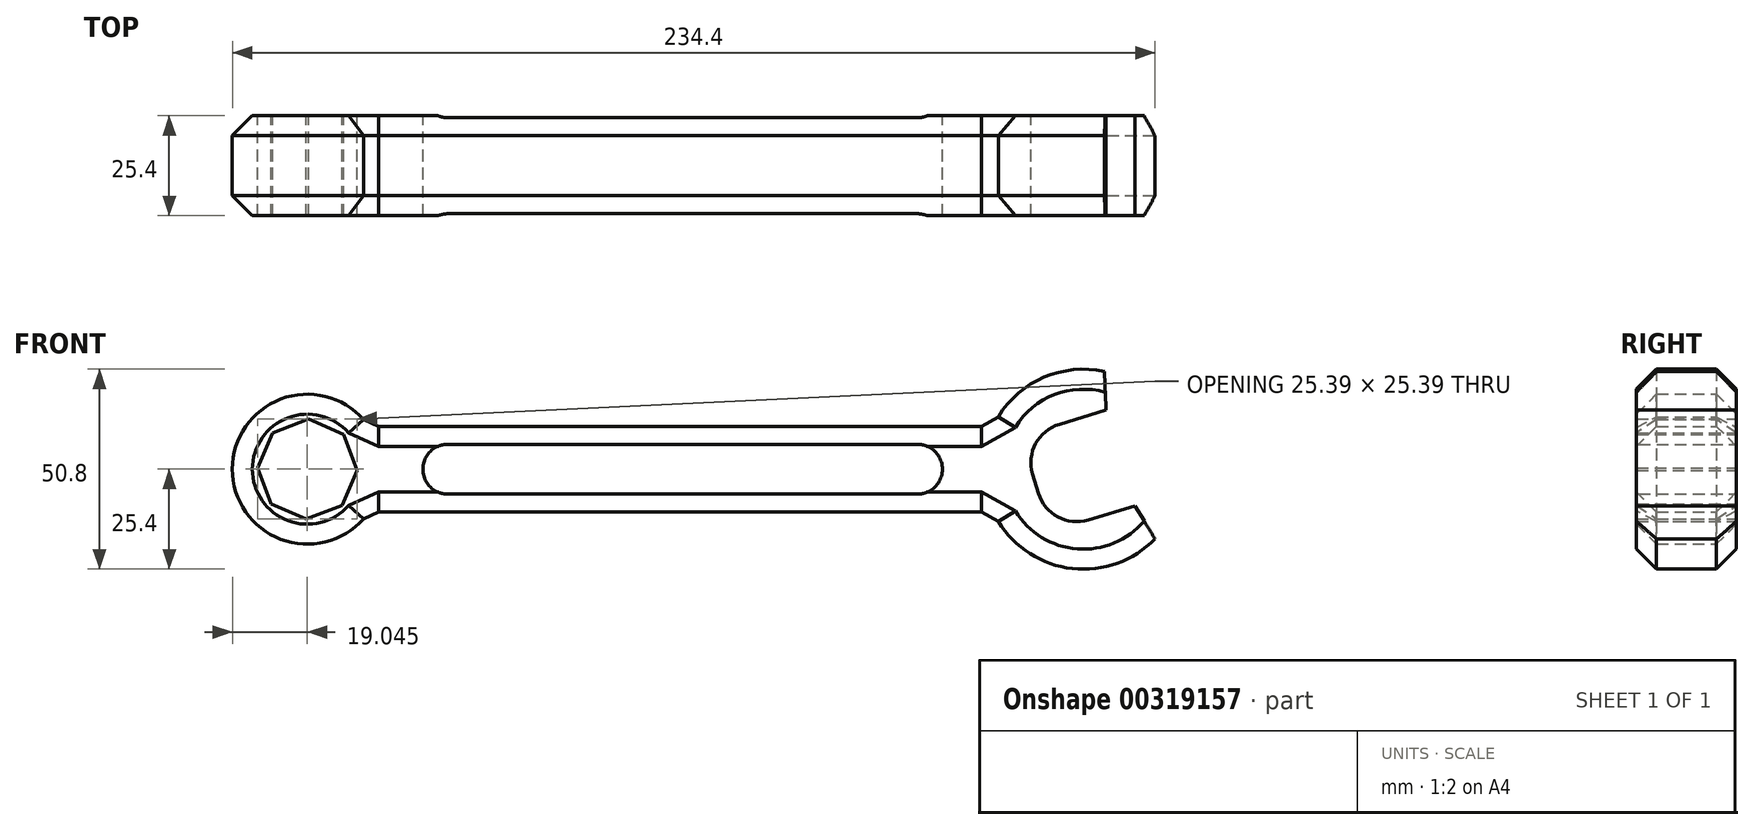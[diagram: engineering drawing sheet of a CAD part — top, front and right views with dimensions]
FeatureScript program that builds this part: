
annotation { "Feature Type Name" : "Feature", "Feature Type Description" : "" }
export const myFeature = defineFeature(function(context is Context, id is Id, definition is map)
    precondition{}
    {
        {
            var Q0;
            Q0=qCreatedBy(makeId("Front.planeOp"),FACE);
            var sketch = newSketch(context, id + "F0", { "sketchPlane" : qUnion([Q0])});
            skCircle(sketch, "E0", {"center": v(-95.33, 0) * mm, "radius": 19.05 * mm});
            skArc(sketch, "E1", {"start": v(119.2, 18.52) * mm, "mid": v(77.5, -7.35) * mm, "end": v(126.55, -5.8) * mm});
            skLineSegment(sketch, "E2", {"start": v(-79.71, 10.9) * mm, "end": v(78.88, 10.9) * mm});
            skLineSegment(sketch, "E3.MirrorCS", {"start": v(-79.71, -10.9) * mm, "end": v(78.88, -10.9) * mm});
            skCircle(sketch, "E4.cCircle", {"center": v(-95.33, 0) * mm, "radius": 12.7 * mm, "construction": true});
            skLineSegment(sketch, "E4.0", {"start": v(-86.54, -9.16) * mm, "end": v(-95.6, -12.7) * mm});
            skLineSegment(sketch, "E4.1", {"start": v(-95.6, -12.7) * mm, "end": v(-104.5, -8.8) * mm});
            skLineSegment(sketch, "E4.2", {"start": v(-104.5, -8.8) * mm, "end": v(-108.03, 0.26) * mm});
            skLineSegment(sketch, "E4.3", {"start": v(-108.03, 0.26) * mm, "end": v(-104.13, 9.16) * mm});
            skLineSegment(sketch, "E4.4", {"start": v(-104.13, 9.16) * mm, "end": v(-95.08, 12.7) * mm});
            skLineSegment(sketch, "E4.5", {"start": v(-95.08, 12.7) * mm, "end": v(-86.17, 8.8) * mm});
            skLineSegment(sketch, "E4.6", {"start": v(-86.17, 8.8) * mm, "end": v(-82.64, -0.26) * mm});
            skLineSegment(sketch, "E4.7", {"start": v(-82.64, -0.26) * mm, "end": v(-86.54, -9.16) * mm});
            skArc(sketch, "E5.cCircle", {"start": v(98.14, 12.16) * mm, "mid": v(89.66, -3.68) * mm, "end": v(105.5, -12.16) * mm, "construction": true});
            skLineSegment(sketch, "E5.1", {"start": v(117.65, -8.48) * mm, "end": v(103.06, -12.9) * mm});
            skLineSegment(sketch, "E5.2", {"start": v(90.4, -6.1) * mm, "end": v(88.93, -1.24) * mm});
            skLineSegment(sketch, "E5.3", {"start": v(95.71, 11.42) * mm, "end": v(110.3, 15.83) * mm});
            skPoint(sketch, "E5.0.midPoint", {"position": v(113.97, 3.68) * mm});
            skLineSegment(sketch, "E6", {"start": v(110.3, 15.83) * mm, "end": v(119.2, 18.52) * mm});
            skLineSegment(sketch, "E7", {"start": v(117.65, -8.48) * mm, "end": v(126.55, -5.8) * mm});
            skArc(sketch, "E8", {"start": v(-59.67, 6.33) * mm, "mid": v(-66, 0) * mm, "end": v(-59.67, -6.33) * mm});
            skLineSegment(sketch, "E9", {"start": v(-59.67, 6.33) * mm, "end": v(59.71, 6.33) * mm});
            skLineSegment(sketch, "E10", {"start": v(-59.67, -6.33) * mm, "end": v(59.71, -6.33) * mm});
            skPoint(sketch, "E11.visualSharp", {"position": v(85.99, 8.48) * mm});
            skArc(sketch, "E11.filletArc", {"start": v(95.71, 11.42) * mm, "mid": v(89.7, 6.5) * mm, "end": v(88.93, -1.24) * mm});
            skPoint(sketch, "E12.visualSharp", {"position": v(93.34, -15.83) * mm});
            skArc(sketch, "E12.filletArc", {"start": v(90.4, -6.1) * mm, "mid": v(95.32, -12.12) * mm, "end": v(103.06, -12.9) * mm});
            skText(sketch, "E13", { "text": "M.B.P.", "fontName": "OpenSans-Regular.ttf"});
            skArc(sketch, "E14.MirrorCS", {"start": v(59.67, 6.33) * mm, "mid": v(66, 0) * mm, "end": v(59.67, -6.33) * mm});
            const initialGuessF0  = {"E13": [-0.01664, -0.00413, 1, 0, 0.00815]};
            skSetInitialGuess(sketch, initialGuessF0);
            skSolve(sketch);
        }
        {
            var Q0;
            Q0 = qSketchRegion(id + "F0", true);
            extrude(context, id + "F1", {"entities" : qUnion([Q0]), "depth" : 25.4 * mm});
        }
        {
            var Q0;
            Q0=makeQuery(id+"F1.opExtrude","SWEPT_FACE",FACE,{"disambiguationData":[OSD([sQuery(id+"F0.wireOp",EDGE,"E2")])]});
            var Q1;
            Q1=makeQuery(id+"F1.opExtrude","SWEPT_FACE",FACE,{"disambiguationData":[OSD([sQuery(id+"F0.wireOp",EDGE,"E0")])]});
            var Q2;
            Q2=makeQuery(id+"F1.opExtrude","SWEPT_FACE",FACE,{"disambiguationData":[OSD([sQuery(id+"F0.wireOp",EDGE,"E3.MirrorCS")])]});
            var Q3;
            {var subQ0=sQuery(id+"F0.wireOp",EDGE,"E1");Q3=makeQuery(id+"F1.opExtrude","SWEPT_FACE",FACE,{"disambiguationData":[OSD([subQ0]),TDD([makeQuery(id+"F0.imprint","IMPRINT",EDGE,{"disambiguationData":[TD([[makeQuery(id+"F0.imprint","INTERSECT",VERTEX,{"derivedFrom":[subQ0,sQuery(id+"F0.wireOp",EDGE,"E7")]}),1.0]])],"derivedFrom":subQ0})])]});}
            var Q4;
            {var subQ0=sQuery(id+"F0.wireOp",EDGE,"E1");Q4=makeQuery(id+"F1.opExtrude","SWEPT_FACE",FACE,{"disambiguationData":[OSD([subQ0]),TDD([makeQuery(id+"F0.imprint","IMPRINT",EDGE,{"disambiguationData":[TD([[makeQuery(id+"F0.imprint","INTERSECT",VERTEX,{"derivedFrom":[subQ0,sQuery(id+"F0.wireOp",EDGE,"E6")]}),-1.0]])],"derivedFrom":subQ0})])]});}
            chamfer(context, id + "F2", {"entities" : qUnion([Q0, Q1, Q2, Q3, Q4]), "width" : 5.08 * mm, "tangentPropagation" : true});
        }
    });
